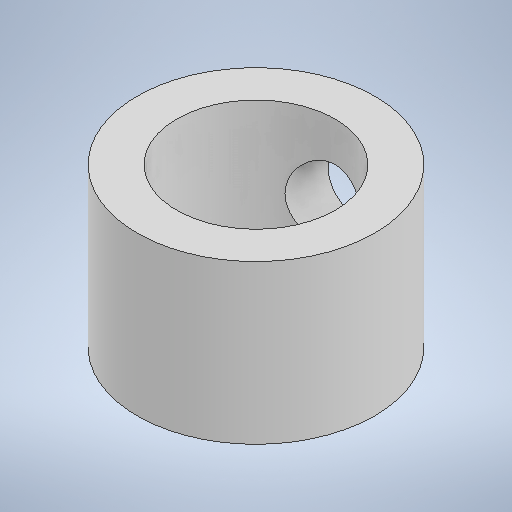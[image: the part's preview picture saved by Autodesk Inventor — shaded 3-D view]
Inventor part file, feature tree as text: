
AUTODESK INVENTOR PART (.ipt)
format: ipt  version: 2025.1 (Build 291241000, 241)  size: 211,456 bytes
history: native  units: mm
features: sketch x2, extrude x1, plane x1, hole x1
ambient origin geometry x8: Origin, YZ Plane, XZ Plane, XY Plane, X Axis, Y Axis, Z Axis, Center Point
bodies: Solid1 (feature_tree)
feature tree (5):
  extrude  "Extrusion1"  Depth=4.0mm
  plane  "Work Plane1"
  hole  "Hole1"  [1 undecoded]
  sketch  "Sketch1"  dims[d0=6.0mm d1=4.0mm]
  sketch  "Sketch2"  dims[d2=4.0mm d3=0.0mm d4=3.0mm d5=2.0mm d6=6.0mm d7=4.0mm d8=2.0mm d9=90.0deg d10=1.4mm d11=0.0mm]
note: 1 required parameter value undecoded (feature->parameter linkage not recoverable at this tier; creation-order binding heuristic only, values carry confidence <= 0.55)
